# Revit family: 05-9885-Z5-CL
name_source: partatom
category: Luminarias
revit_build: Autodesk Revit 2017 (Build: 20160225_1515(x64)
units: mm (PartAtom-declared; Revit-internal decimal feet)

## family parameters
Anfitrión = Cara
Compartido = Sí
Corte con vacíos al cargar = No
Cota de conector redondo = Diámetro de uso
Número OmniClass = 23.80.70.00
Origen de luz = No
Punto de cálculo de habitación = No
Tipo de pieza = Normal
Título OmniClass = Lighting

## types (1)
- 05-9885-Z5-CL
    Acabado = Gris urbano, Semi arenado
    CRI = 80
    Carga aparente = 0 VA
    Catálogo = Outdoor
    CodigoGubimclass = 50.60.50.20
    CodigoOmniclass = 21-04 50 40
    CodigoUniclass2015 = EF_70_80
    CodigoUniformat2010 = D5040
    DescripcionGubimclass = Iluminación interior
    DescripcionOmniclass = Lighting
    DescripcionUniclass2015 = Lighting
    DescripcionUniformat2010 = Lighting
    EAN13 = 8435381454739
    Eficiencia energética = LED A++
    Elevación por defecto = 1000 mm  [stored 3.28084 ft]
    Etiqueta V/f = 100-240V/50-60Hz
    Fabricante = LEDS C4
    Familia = Micenas LED Square
    FechaVersion = Julio 2020
    Ficha = http://files.leds-c4.com
    Fotometría = http://files.leds-c4.com
    Fuente de luz = 18xLED 20 1862.00 lm
    IK = IK10
    IMC = http://files.leds-c4.com
    IP = IP65
    IfcExportAs = IfcLightFixture
IfcLightFixture
    IfcExportType = NOTDEFINED
    Imagen web = http://files.leds-c4.com
    LDT = http://files.leds-c4.com
    Lumenes reales (lm) = 504
    Material = Aluminio, Cristal
    Peso neto (KG) = 2.12
    Pluma comercial = http://files.leds-c4.com
    Producto descatalogado = Catalogado ES
    Rayo de luz = Check Photometric file
    Referencia = 05-9885-Z5-CL
    Temperatura color led (K) = Blanco cálido - 3000K
    Tender text (Castellano) = LEDS C4
Micenas LED Square
05-9885-Z5-CL

Empotrado de pared de uso exterior para iluminar frontalmente y hacia abajo. 

Incluye caja de empotrar. Incluye 2 salidas de cable para facilitar la instalación en cadena. Material estructura: Aluminio. Acabado estructura: Gris urbano. Material difusor: Cristal. Acabado difusor: Semi arenado. Protección contra los rayos ultravioleta. Garantía: 5 Años.

Peso neto del producto (Kg): 2.120
Anchura o diámetro del producto (mm): 250
Altura del producto (mm): 265
Salida del producto (mm): 91

Clase 1. Prueba hilo incandescente: 850. IP: IP65. IK: IK10. LED. Nº de portalámparas o Leds: 18. Marca del LED: OSRAM. Marca del Driver: EAGLERISE. Potencia máxima de la fuente de luz: 20W. Temperatura de color: Blanco cálido - 3000K. Índice de reproducción cromática: 80. Steps Mac Adam: 3. Diámetro máximo de la bombilla que admite la luminaria: 50.000h L80B20. Riesgo fotobiológico: RG1. Flujo real (lm): 504. Flujo nominal (lm): 1862. Lm/W reales: 22. Rango de voltaje/frecuencia: 100-240 VAC. Voltaje: 6. Equipo incluido: Si, electrónico. Equipo multivoltaje incluido. Potencia total: 22.5. Factor de potencia: 0.96.
    Tender text (English) = LEDS C4
Micenas LED Square
05-9885-Z5-CL

Wall recessed for outdoor use. 

For frontal lighting and downlighting. Includes flush-mounting box. Includes 2 cable outlets to facilitate chain mounting. Structure material: Aluminium. Structure finish: Urban grey. Diffuser material: Glass. Diffuser finish: Partly-sandblasted. UV protection. Warranty: 5 Years.

Product net weight (Kg): 2.120
Product width or diameter (mm): 250
Product height (mm): 265
Product aperture (mm): 91

Class 1. Glow wire test: 850. IP: IP65. IK: IK10. LED. No. of lampholders or LEDs: 18. LED brand: OSRAM. Driver brand: EAGLERISE. Maximum power of light source: 20W. Colour temperature: LED warm-white 3000K. Colour rendering index: 80. MacAdam Steps: 3. Maximum diameter of luminaire bulb: 50.000h L80B20. Photobiological risk: RG1. Real flux (lm): 504. Nominal flux (lm): 1862. Lm/Real W: 22. Voltage and frequency range: 100-240 VAC. Voltage: 6. Gear included: Yes, electronic. Multi-voltage gear included. Total power: 22.5. Power factor: 0.96.
    Tipo = Empotrable de pared
    Vatios (W) = 22.5
    Versión = v1

note: [stored X ft] marks values corroborated as IEEE doubles in the binary element streams (Revit-internal decimal feet)
